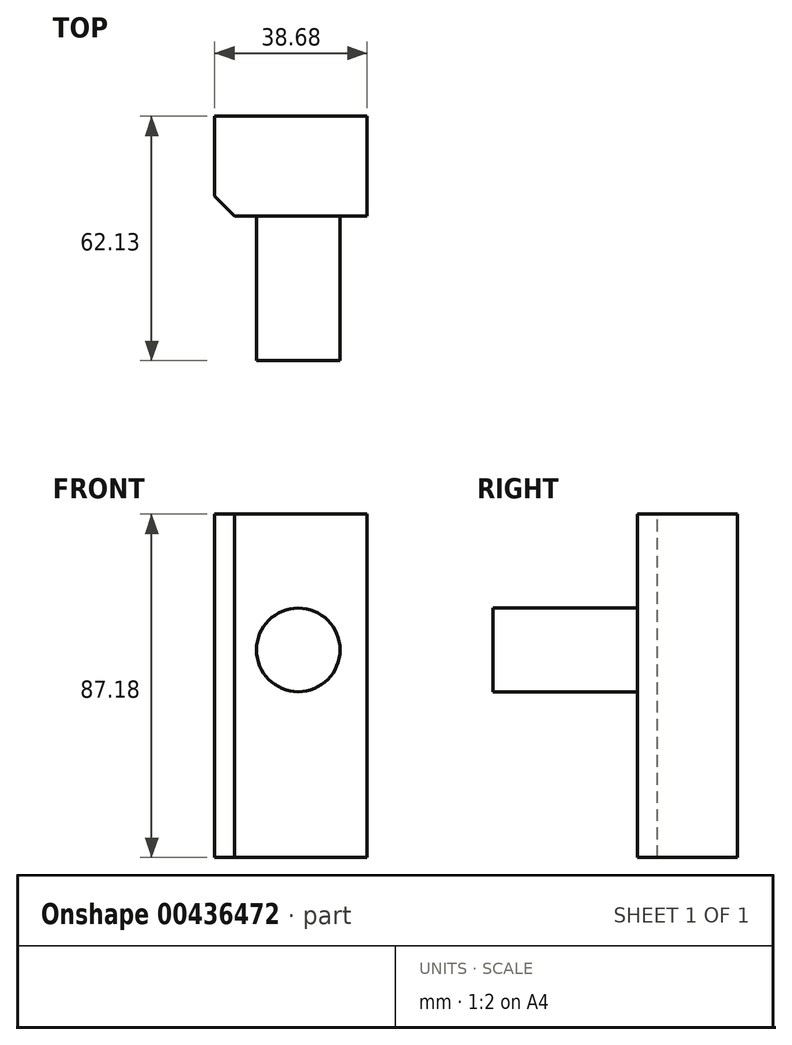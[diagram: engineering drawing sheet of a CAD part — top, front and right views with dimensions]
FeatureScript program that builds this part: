
annotation { "Feature Type Name" : "Feature", "Feature Type Description" : "" }
export const myFeature = defineFeature(function(context is Context, id is Id, definition is map)
    precondition{}
    {
        {
            var Q0;
            Q0=qCreatedBy(makeId("Front.planeOp"),FACE);
            var sketch = newSketch(context, id + "F0", { "sketchPlane" : qUnion([Q0])});
            skLineSegment(sketch, "E0.bottom", {"start": v(59.02, 48.95) * mm, "end": v(20.34, 48.95) * mm});
            skLineSegment(sketch, "E0.top", {"start": v(59.02, -38.23) * mm, "end": v(20.34, -38.23) * mm});
            skLineSegment(sketch, "E0.left", {"start": v(59.02, 48.95) * mm, "end": v(59.02, -38.23) * mm});
            skLineSegment(sketch, "E0.right", {"start": v(20.34, 48.95) * mm, "end": v(20.34, -38.23) * mm});
            skSolve(sketch);
        }
        {
            var Q0;
            Q0=makeQuery(id+"F0.imprint","IMPRINT",FACE,{"disambiguationData":[TD([[makeQuery(id+"F0.imprint","IMPRINT",EDGE,{"derivedFrom":sQuery(id+"F0.wireOp",EDGE,"E0.bottom")}),1.0]])]});
            extrude(context, id + "F1", {"entities" : qUnion([Q0]), "depth" : 25.4 * mm});
        }
        {
            var Q0;
            Q0=makeQuery(id+"F1.opExtrude","CAP_FACE",FACE,{"disambiguationData":[OSD([sQuery(id+"F0.wireOp",EDGE,"E0.bottom"),sQuery(id+"F0.wireOp",EDGE,"E0.top"),sQuery(id+"F0.wireOp",EDGE,"E0.left"),sQuery(id+"F0.wireOp",EDGE,"E0.right")])],"isStart":false});
            var sketch = newSketch(context, id + "F2", { "sketchPlane" : qUnion([Q0])});
            skCircle(sketch, "E1", {"center": v(41.56, 14.47) * mm, "radius": 10.61 * mm});
            skSolve(sketch);
        }
        {
            var Q0;
            Q0 = qSketchRegion(id + "F2", true);
            extrude(context, id + "F3", {"entities" : qUnion([Q0]), "operationType" : NewBodyOperationType.ADD, "depth" : 36.73 * mm});
        }
        {
            var Q0;
            Q0=makeQuery(id+"F1.opExtrude","CAP_EDGE",EDGE,{"disambiguationData":[OSD([sQuery(id+"F0.wireOp",EDGE,"E0.right")])],"isStart":false});
            chamfer(context, id + "F4", {"entities" : qUnion([Q0]), "width" : 5.08 * mm, "tangentPropagation" : true});
        }
    });
